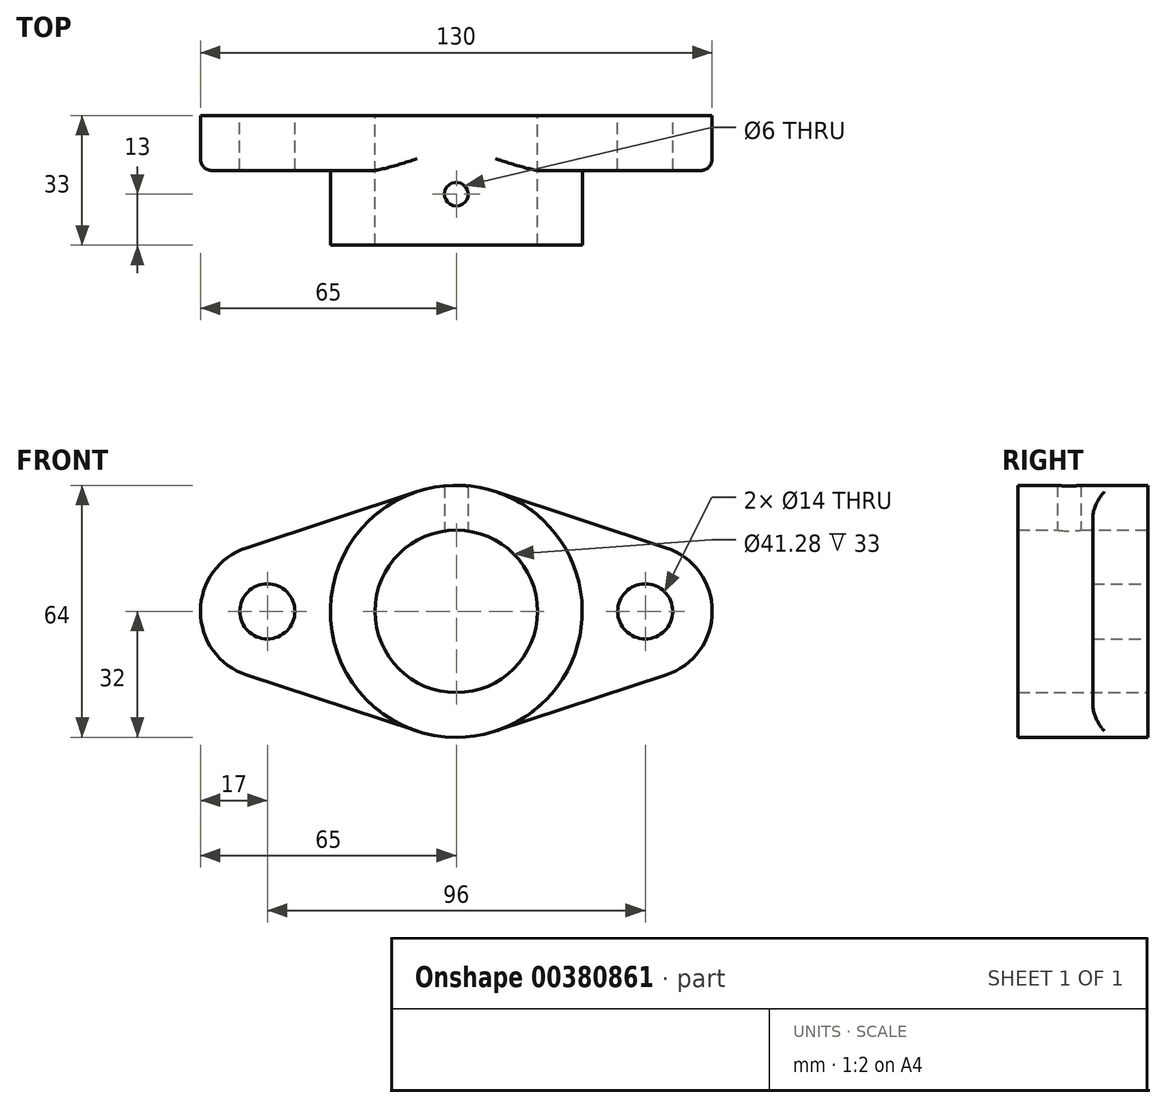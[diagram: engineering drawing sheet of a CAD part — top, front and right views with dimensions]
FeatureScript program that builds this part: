
annotation { "Feature Type Name" : "Feature", "Feature Type Description" : "" }
export const myFeature = defineFeature(function(context is Context, id is Id, definition is map)
    precondition{}
    {
        {
            var Q0;
            Q0=qCreatedBy(makeId("Front.planeOp"),FACE);
            var sketch = newSketch(context, id + "F0", { "sketchPlane" : qUnion([Q0])});
            skCircle(sketch, "E0", {"center": v(0, 0) * mm, "radius": 32 * mm});
            skCircle(sketch, "E1", {"center": v(-48, 0) * mm, "radius": 7 * mm});
            skCircle(sketch, "E2", {"center": v(48, 0) * mm, "radius": 7 * mm});
            skCircle(sketch, "E3", {"center": v(0, 0) * mm, "radius": 20.64 * mm});
            skArc(sketch, "E4", {"start": v(-53.31, 16.15) * mm, "mid": v(-65, 0) * mm, "end": v(-53.31, -16.15) * mm});
            skArc(sketch, "E5", {"start": v(53.31, -16.15) * mm, "mid": v(65, 0) * mm, "end": v(53.31, 16.15) * mm});
            skLineSegment(sketch, "E6", {"start": v(-53.31, 16.15) * mm, "end": v(-10, 30.4) * mm});
            skLineSegment(sketch, "E7", {"start": v(53.31, 16.15) * mm, "end": v(10, 30.4) * mm});
            skLineSegment(sketch, "E8", {"start": v(53.31, -16.15) * mm, "end": v(10, -30.4) * mm});
            skLineSegment(sketch, "E9", {"start": v(-10, -30.4) * mm, "end": v(-53.31, -16.15) * mm});
            skSolve(sketch);
        }
        {
            var Q0;
            Q0=makeQuery(id+"F0.imprint","IMPRINT",FACE,{"disambiguationData":[TD([[makeQuery(id+"F0.imprint","IMPRINT",EDGE,{"derivedFrom":sQuery(id+"F0.wireOp",EDGE,"E3")}),-1.0]])]});
            extrude(context, id + "F1", {"entities" : qUnion([Q0]), "depth" : 33 * mm});
        }
        {
            var Q0;
            Q0=makeQuery(id+"F0.imprint","IMPRINT",FACE,{"disambiguationData":[TD([[makeQuery(id+"F0.imprint","IMPRINT",EDGE,{"derivedFrom":sQuery(id+"F0.wireOp",EDGE,"E1")}),-1.0]])]});
            var Q1;
            Q1=makeQuery(id+"F0.imprint","IMPRINT",FACE,{"disambiguationData":[TD([[makeQuery(id+"F0.imprint","IMPRINT",EDGE,{"derivedFrom":sQuery(id+"F0.wireOp",EDGE,"E2")}),-1.0]])]});
            extrude(context, id + "F2", {"entities" : qUnion([Q0, Q1]), "operationType" : NewBodyOperationType.ADD, "depth" : 14 * mm});
        }
        {
            var Q0;
            Q0=qCreatedBy(makeId("Top.planeOp"),FACE);
            var sketch = newSketch(context, id + "F3", { "sketchPlane" : qUnion([Q0])});
            skCircle(sketch, "E10", {"center": v(0, -20) * mm, "radius": 3 * mm});
            skSolve(sketch);
        }
        {
            var Q0;
            Q0=makeQuery(id+"F3.imprint","IMPRINT",FACE,{"disambiguationData":[TD([[makeQuery(id+"F3.imprint","IMPRINT",EDGE,{"derivedFrom":sQuery(id+"F3.wireOp",EDGE,"E10")}),1.0]])]});
            extrude(context, id + "F4", {"entities" : qUnion([Q0]), "operationType" : NewBodyOperationType.REMOVE, "endBound" : BoundingType.THROUGH_ALL, "depth" : 25 * mm});
        }
        {
            var Q0;
            Q0=makeQuery(id+"F2.opExtrude","CAP_EDGE",EDGE,{"disambiguationData":[OSD([sQuery(id+"F0.wireOp",EDGE,"E6")])],"isStart":false});
            var Q1;
            Q1=makeQuery(id+"F2.opExtrude","CAP_EDGE",EDGE,{"disambiguationData":[OSD([sQuery(id+"F0.wireOp",EDGE,"E4")])],"isStart":false});
            var Q2;
            Q2=makeQuery(id+"F2.opExtrude","CAP_EDGE",EDGE,{"disambiguationData":[OSD([sQuery(id+"F0.wireOp",EDGE,"E9")])],"isStart":false});
            var Q3;
            Q3=makeQuery(id+"F2.opExtrude","CAP_EDGE",EDGE,{"disambiguationData":[OSD([sQuery(id+"F0.wireOp",EDGE,"E8")])],"isStart":false});
            var Q4;
            Q4=makeQuery(id+"F2.opExtrude","CAP_EDGE",EDGE,{"disambiguationData":[OSD([sQuery(id+"F0.wireOp",EDGE,"E5")])],"isStart":false});
            var Q5;
            Q5=makeQuery(id+"F2.opExtrude","CAP_EDGE",EDGE,{"disambiguationData":[OSD([sQuery(id+"F0.wireOp",EDGE,"E7")])],"isStart":false});
            var Q6;
            {var subQ0=sQuery(id+"F0.wireOp",EDGE,"E0");Q6=makeQuery(id+"F2.opExtrude","CAP_EDGE",EDGE,{"disambiguationData":[OSD([subQ0]),TDD([makeQuery(id+"F0.imprint","IMPRINT",EDGE,{"disambiguationData":[TD([[makeQuery(id+"F0.imprint","INTERSECT",VERTEX,{"derivedFrom":[subQ0,sQuery(id+"F0.wireOp",EDGE,"E7")]}),1.0]])],"derivedFrom":subQ0})])],"isStart":false});}
            var Q7;
            {var subQ0=sQuery(id+"F0.wireOp",EDGE,"E0");Q7=makeQuery(id+"F2.opExtrude","CAP_EDGE",EDGE,{"disambiguationData":[OSD([subQ0]),TDD([makeQuery(id+"F0.imprint","IMPRINT",EDGE,{"disambiguationData":[TD([[makeQuery(id+"F0.imprint","INTERSECT",VERTEX,{"derivedFrom":[subQ0,sQuery(id+"F0.wireOp",EDGE,"E6")]}),-1.0]])],"derivedFrom":subQ0})])],"isStart":false});}
            fillet(context, id + "F5", {"entities" : qUnion([Q0, Q1, Q2, Q3, Q4, Q5, Q6, Q7]), "radius" : 3 * mm, "tangentPropagation" : true, "allowEdgeOverflow" : false});
        }
    });
